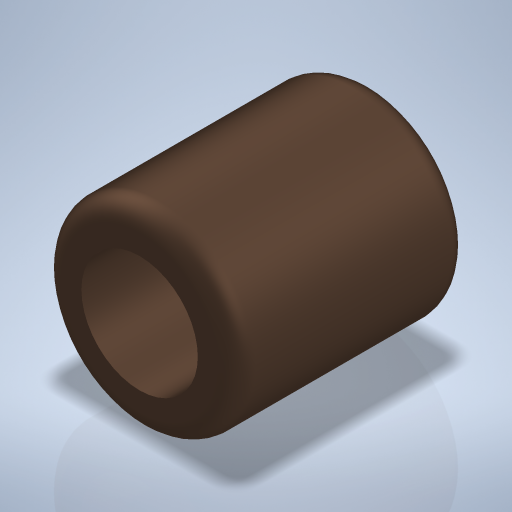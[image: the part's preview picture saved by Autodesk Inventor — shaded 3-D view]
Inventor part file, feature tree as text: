
AUTODESK INVENTOR PART (.ipt)
format: ipt  version: 2024 (Build 280153000, 153)  size: 254,976 bytes
history: native  units: mm
features: extrude x1, fillet x1, sketch x1
ambient origin geometry x8: Origin, YZ Plane, XZ Plane, XY Plane, X Axis, Y Axis, Z Axis, Center Point
bodies: Volumenkörper1 (feature_tree)
feature tree (3):
  extrude  "Extrusion1"  Depth=6.0mm
  fillet  "Rundung1"  Radius=12.0mm
  sketch  "Skizze1"  dims[d0=10.0mm d1=6.0mm d2=12.0mm d3=0.0mm d4=1.0mm]
